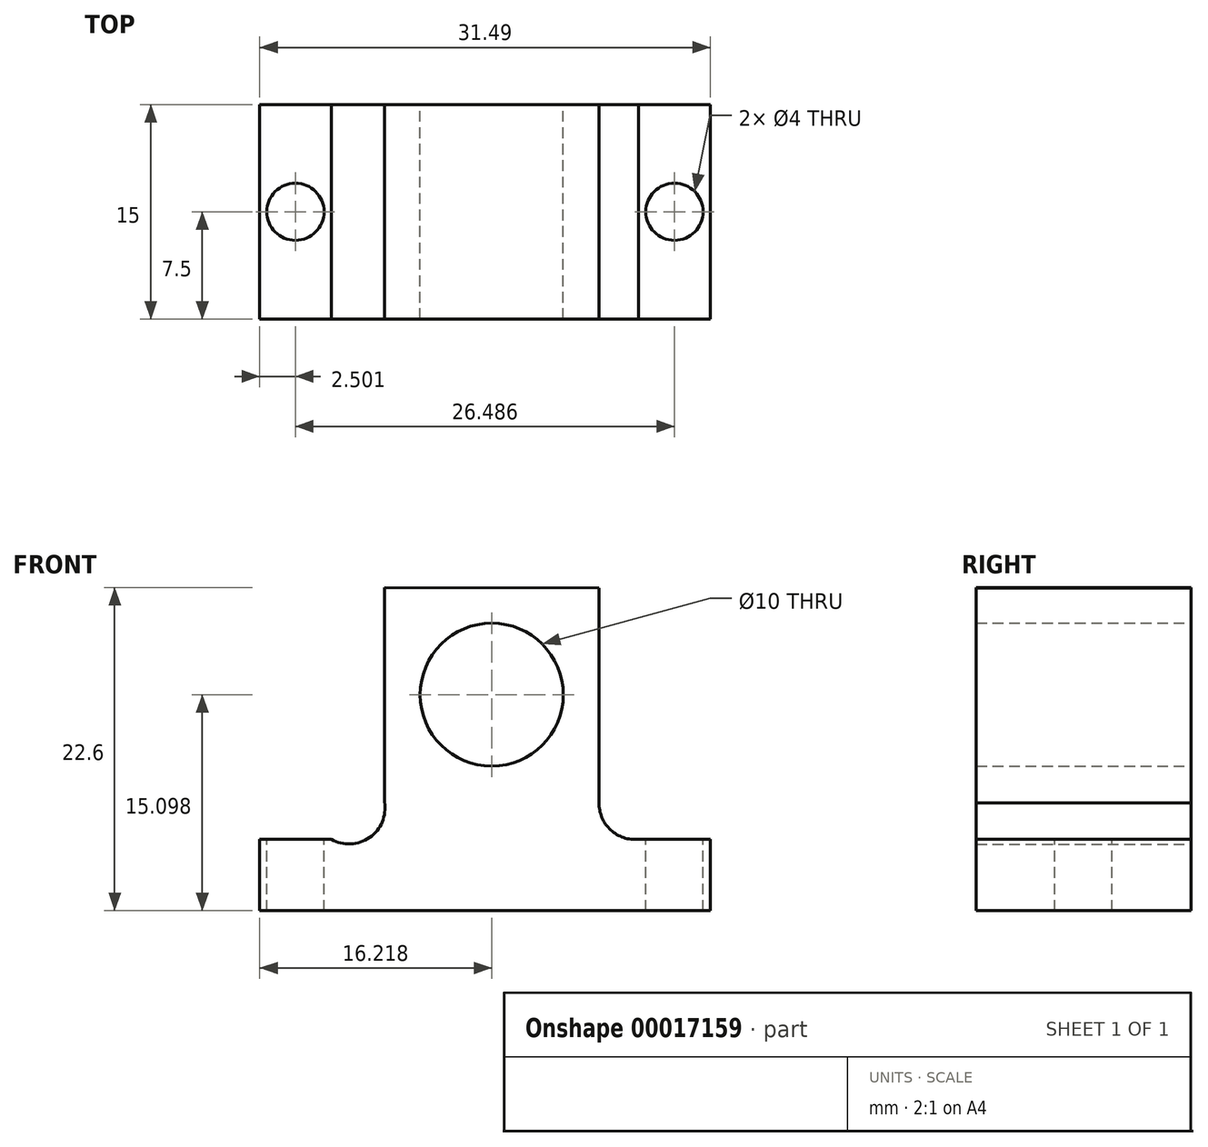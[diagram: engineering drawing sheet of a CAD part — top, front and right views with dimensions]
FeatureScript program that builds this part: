
annotation { "Feature Type Name" : "Feature", "Feature Type Description" : "" }
export const myFeature = defineFeature(function(context is Context, id is Id, definition is map)
    precondition{}
    {
        {
            var Q0;
            Q0=qCreatedBy(makeId("Front.planeOp"),FACE);
            var sketch = newSketch(context, id + "F0", { "sketchPlane" : qUnion([Q0])});
            skLineSegment(sketch, "E0", {"start": v(-12.6, -3.64) * mm, "end": v(18.88, -3.64) * mm});
            skLineSegment(sketch, "E1", {"start": v(18.88, -3.64) * mm, "end": v(18.88, 1.36) * mm});
            skLineSegment(sketch, "E2", {"start": v(18.88, 1.36) * mm, "end": v(13.88, 1.36) * mm});
            skLineSegment(sketch, "E3", {"start": v(-12.6, -3.64) * mm, "end": v(-12.6, 1.36) * mm});
            skLineSegment(sketch, "E4", {"start": v(-12.6, 1.36) * mm, "end": v(-7.6, 1.36) * mm});
            skArc(sketch, "E5", {"start": v(-7.6, 1.36) * mm, "mid": v(-4.92, 1.47) * mm, "end": v(-3.9, 3.96) * mm});
            skArc(sketch, "E6", {"start": v(11.1, 3.9) * mm, "mid": v(11.92, 2) * mm, "end": v(13.88, 1.36) * mm});
            skLineSegment(sketch, "E7", {"start": v(11.1, 3.9) * mm, "end": v(11.1, 18.9) * mm});
            skLineSegment(sketch, "E8", {"start": v(-3.9, 3.96) * mm, "end": v(-3.9, 18.96) * mm});
            skLineSegment(sketch, "E9", {"start": v(-3.9, 18.96) * mm, "end": v(11.1, 18.9) * mm});
            skCircle(sketch, "E10", {"center": v(3.6, 11.46) * mm, "radius": 5 * mm});
            skSolve(sketch);
        }
        {
            var Q0;
            Q0 = qSketchRegion(id + "F0", true);
            extrude(context, id + "F1", {"entities" : qUnion([Q0]), "depth" : 15 * mm});
        }
        {
            var Q0;
            Q0=makeQuery(id+"F1.opExtrude","SWEPT_FACE",FACE,{"disambiguationData":[OSD([sQuery(id+"F0.wireOp",EDGE,"E2")])]});
            var sketch = newSketch(context, id + "F2", { "sketchPlane" : qUnion([Q0])});
            skCircle(sketch, "E11", {"center": v(16.38, -7.5) * mm, "radius": 2 * mm});
            skSolve(sketch);
        }
        {
            var Q0;
            Q0=makeQuery(id+"F2.imprint","IMPRINT",FACE,{"disambiguationData":[TD([[makeQuery(id+"F2.imprint","IMPRINT",EDGE,{"derivedFrom":sQuery(id+"F2.wireOp",EDGE,"E11")}),1.0]])]});
            extrude(context, id + "F3", {"entities" : qUnion([Q0]), "operationType" : NewBodyOperationType.REMOVE, "endBound" : BoundingType.THROUGH_ALL, "oppositeDirection" : true, "depth" : 25 * mm});
        }
        {
            var Q0;
            Q0=makeQuery(id+"F1.opExtrude","SWEPT_FACE",FACE,{"disambiguationData":[OSD([sQuery(id+"F0.wireOp",EDGE,"E4")])]});
            var sketch = newSketch(context, id + "F4", { "sketchPlane" : qUnion([Q0])});
            skCircle(sketch, "E12", {"center": v(-10.1, -7.5) * mm, "radius": 2 * mm});
            skSolve(sketch);
        }
        {
            var Q0;
            Q0=makeQuery(id+"F4.imprint","IMPRINT",FACE,{"disambiguationData":[TD([[makeQuery(id+"F4.imprint","IMPRINT",EDGE,{"derivedFrom":sQuery(id+"F4.wireOp",EDGE,"E12")}),1.0]])]});
            extrude(context, id + "F5", {"entities" : qUnion([Q0]), "operationType" : NewBodyOperationType.REMOVE, "endBound" : BoundingType.THROUGH_ALL, "oppositeDirection" : true, "depth" : 25 * mm});
        }
    });
